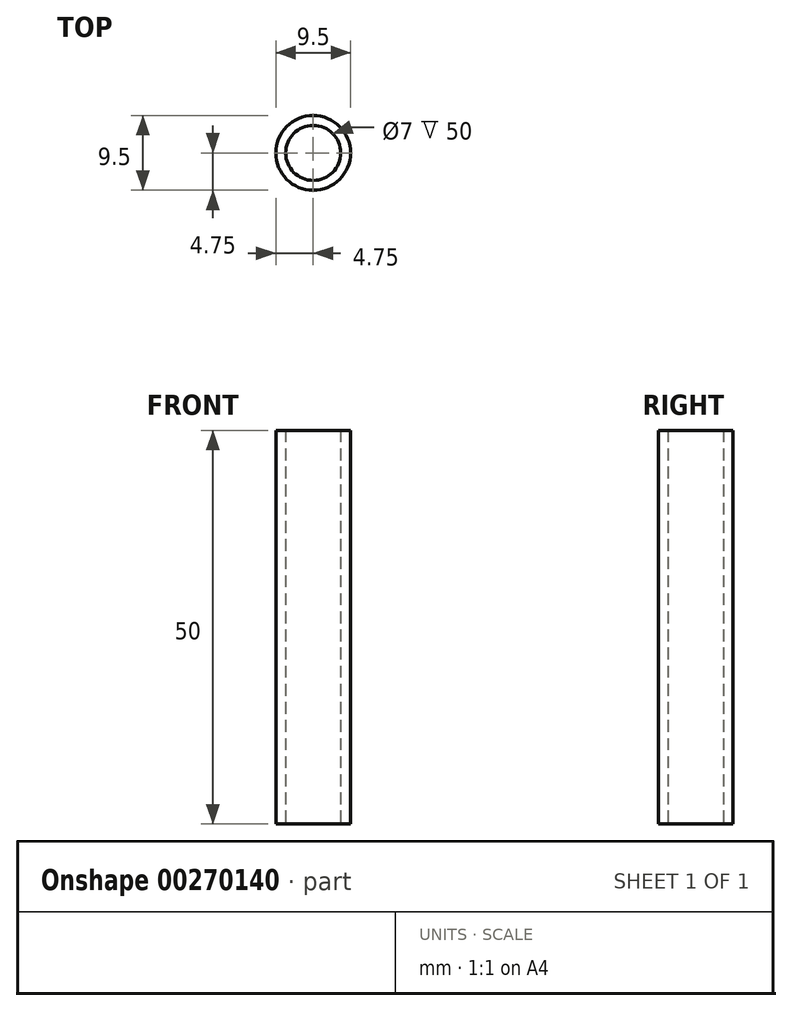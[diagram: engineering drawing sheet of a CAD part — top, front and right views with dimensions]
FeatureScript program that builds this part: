
annotation { "Feature Type Name" : "Feature", "Feature Type Description" : "" }
export const myFeature = defineFeature(function(context is Context, id is Id, definition is map)
    precondition{}
    {
        {
            var Q0;
            Q0=qCreatedBy(makeId("Top.planeOp"),FACE);
            var sketch = newSketch(context, id + "F0", { "sketchPlane" : qUnion([Q0])});
            skCircle(sketch, "E0", {"center": v(0, 0) * mm, "radius": 4.75 * mm});
            skCircle(sketch, "E1", {"center": v(0, 0) * mm, "radius": 3.5 * mm});
            skSolve(sketch);
        }
        {
            var Q0;
            Q0 = qSketchRegion(id + "F0", true);
            extrude(context, id + "F1", {"entities" : qUnion([Q0]), "depth" : 50 * mm});
        }
    });
